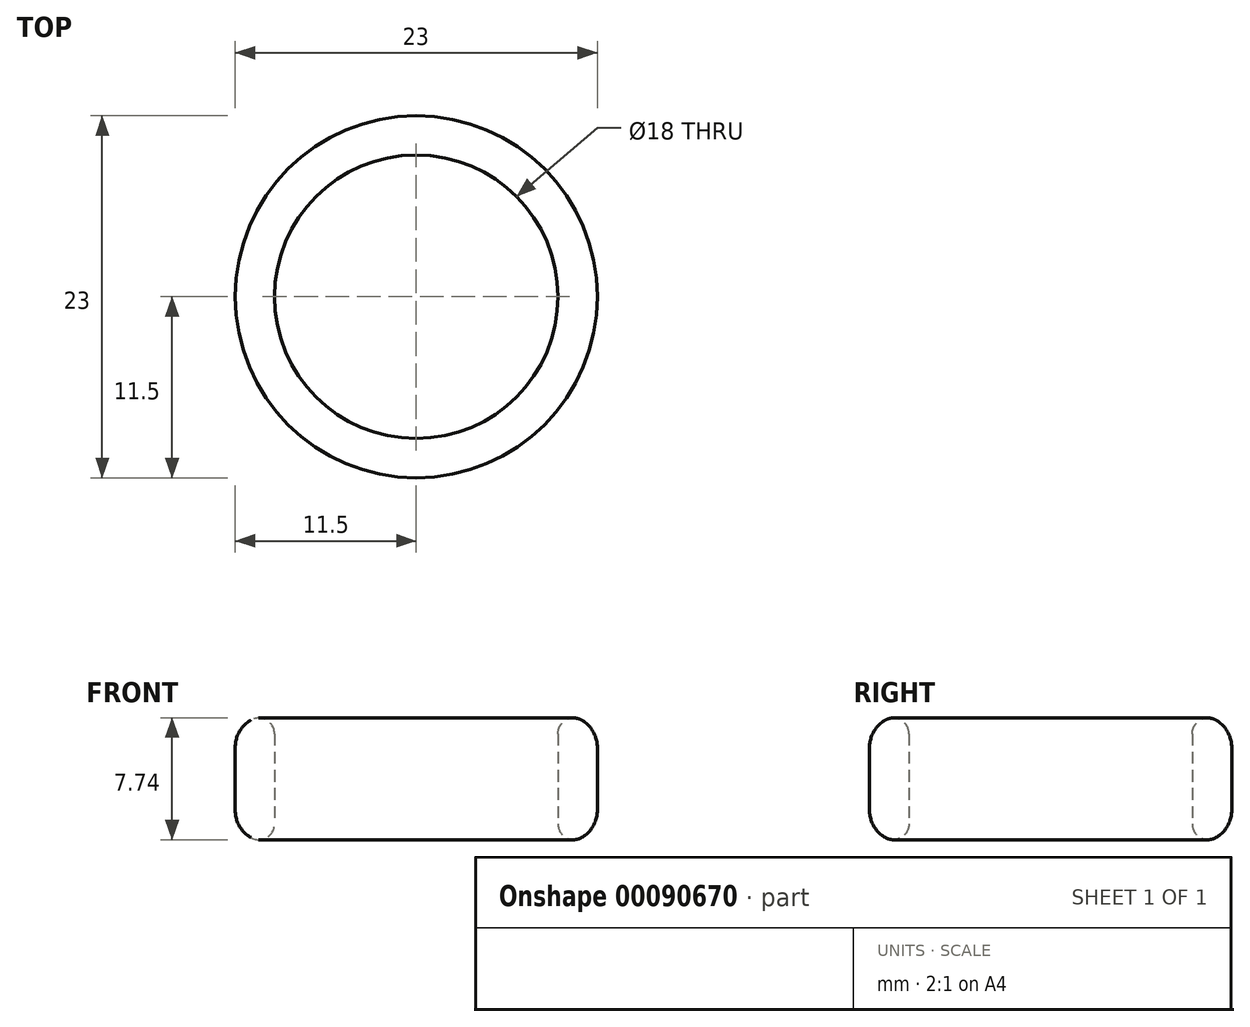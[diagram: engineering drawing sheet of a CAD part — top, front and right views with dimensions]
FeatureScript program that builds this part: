
annotation { "Feature Type Name" : "Feature", "Feature Type Description" : "" }
export const myFeature = defineFeature(function(context is Context, id is Id, definition is map)
    precondition{}
    {
        {
            var Q0;
            Q0=qCreatedBy(makeId("Top.planeOp"),FACE);
            var sketch = newSketch(context, id + "F0", { "sketchPlane" : qUnion([Q0])});
            skCircle(sketch, "E0", {"center": v(0, 0) * mm, "radius": 9 * mm});
            skCircle(sketch, "E1", {"center": v(0, 0) * mm, "radius": 11.5 * mm});
            skSolve(sketch);
        }
        {
            var Q0;
            Q0 = qSketchRegion(id + "F0", true);
            extrude(context, id + "F1", {"entities" : qUnion([Q0]), "depth" : 8 * mm});
        }
        {
            var Q0;
            Q0=makeQuery(id+"F1.opExtrude","CAP_EDGE",EDGE,{"disambiguationData":[OSD([sQuery(id+"F0.wireOp",EDGE,"E1")])],"isStart":true});
            var Q1;
            Q1=makeQuery(id+"F1.opExtrude","CAP_EDGE",EDGE,{"disambiguationData":[OSD([sQuery(id+"F0.wireOp",EDGE,"E1")])],"isStart":false});
            fillet(context, id + "F2", {"entities" : qUnion([Q0, Q1]), "radius" : 2 * mm, "tangentPropagation" : true, "allowEdgeOverflow" : false});
        }
        {
            var Q0;
            Q0=makeQuery(id+"F1.opExtrude","CAP_EDGE",EDGE,{"disambiguationData":[OSD([sQuery(id+"F0.wireOp",EDGE,"E0")])],"isStart":true});
            var Q1;
            Q1=makeQuery(id+"F1.opExtrude","CAP_EDGE",EDGE,{"disambiguationData":[OSD([sQuery(id+"F0.wireOp",EDGE,"E0")])],"isStart":false});
            fillet(context, id + "F3", {"entities" : qUnion([Q0, Q1]), "radius" : 1 * mm, "tangentPropagation" : true, "allowEdgeOverflow" : false});
        }
    });
